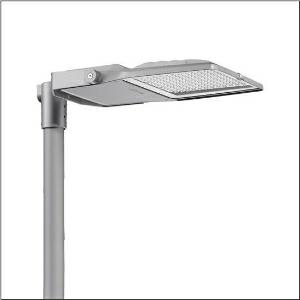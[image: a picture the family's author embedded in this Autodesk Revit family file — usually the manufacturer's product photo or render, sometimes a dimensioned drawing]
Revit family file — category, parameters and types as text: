
# Revit family: floodlight_fl_21_iq_midi___pl33t_5xa7782f4f3a_5715
name_source: partatom
category: Lighting Fixtures
units: mm (PartAtom-declared; Revit-internal decimal feet)

## family parameters
Cut with Voids When Loaded = No
Host = Face
Light Source = No
Part Type = Normal
Room Calculation Point = No
Round Connector Dimension = Use Diameter
Shared = No

## types (1)
- --- (1 x LED, 36900 lm, 270.2 W, 4000K)
    Apparent Load = 270 VA
    CIE Flux Codes = 26 75 99 100 100
    Color Rendering = 70
    Color Temperature = 4000K
    Default Elevation = 1800 mm
    Description = Floodlight FL 21 iQ midi, floodlight, primary light control with lens, of PMMA, primary optical cover: protective disc, of toughened safety glass, transparent, light distribution: PL33T, light emission: direct distribution, installation type: surface-mounted, LED, High Power LED, rated luminous flux: 36.900lm, luminous efficacy: 137lm/W, light colour: 740, colour temperature: 4000K, control gear: iQ Street-Remote/DALI, control: optimised constant luminous flux control (CLO 2.0), Desk-Remote (wireless, voltage-free reading and setting of iQ features in the workshop via application-optimized NFC function/RFID function), Smart-Wire, Night-Set, Temp-Guard, Auto-Match, Street-Remote, with terminal, 6-pole, mains connection: 220..240V, AC, 50/60Hz, start of lifetime: 270W, end of service life: 287W, reduction: 118W, luminaire housing, of diecast aluminium, powder-coated, Siteco® metallic grey (DB 702S), corrosivity category C5 mid according to DIN EN ISO 12944, suitable for swimming pools, chlorine-resistant, sealing non-destructively replaceable, please order mast flange separately, mast bracket, of steel, galvanised, powder-coated, Siteco® metallic grey (DB 702S), protection rating (complete): IP66, insulation class (complete): insulation class II (safety insulation), certification: CE, ENEC, VDE, protection symbol: D, impact resistance: IK08, permissible operating ambient temperature: -40..+40°C, permissible operating ambient temperature for outdoor applications: -40..+50°C, standard: DIN EN 12944, LABS conformity tested according to VDMA 24364:2018-05, packaging unit: 1 piece

Light Distribution: PL33T
    Height = 76 mm
    Lamp = 1 x LED
    Lamp Light Flux = 36900 lm
    Lamp Power = 270.2 W
    Lamp count = 1
    Length = 657 mm
    Luminous efficacy = 137 lm/W
    Manufacturer = Siteco
    ModVariant = No
    Model = 5XA7782F4F3A
    Number of Poles = 1
    OnlyDefault = Yes
    Power Factor = 1
    Product Name = Floodlight FL 21 iQ midi | PL33T
    Product group = floodlight | pylon annexe
    ProductGroupID = 6200
    Protection Class = Protection class II
    Protection Degree = IP 66
    RLX_Detail_Level = 1
    RLX_Emergency_Light_Flux = 0 lm
    RLX_Emergency_Type = 0
    RLX_Emergency_Type_DB = No
    RlxData = <blob elided: 153777 chars, md5=4e818687>
    Socket = socket
    Standby Power = 0 W
    System Light Flux = 36900 lm
    System Power = 270 W
    Type Comments = factory setting: luminous flux: 100 % | dim-lin: 254 | 620 mA
    Type Image = l_1007123.jpg
    URL = http://relux.com
    VarID = @adj_103260
    Voltage = 0 V
    Weight = 0.00 kg
    Width = 442 mm

## geometry (parser evidence)
native form markers: Blend x4, Sweep x14
no freeform markers — native parametric forms only
